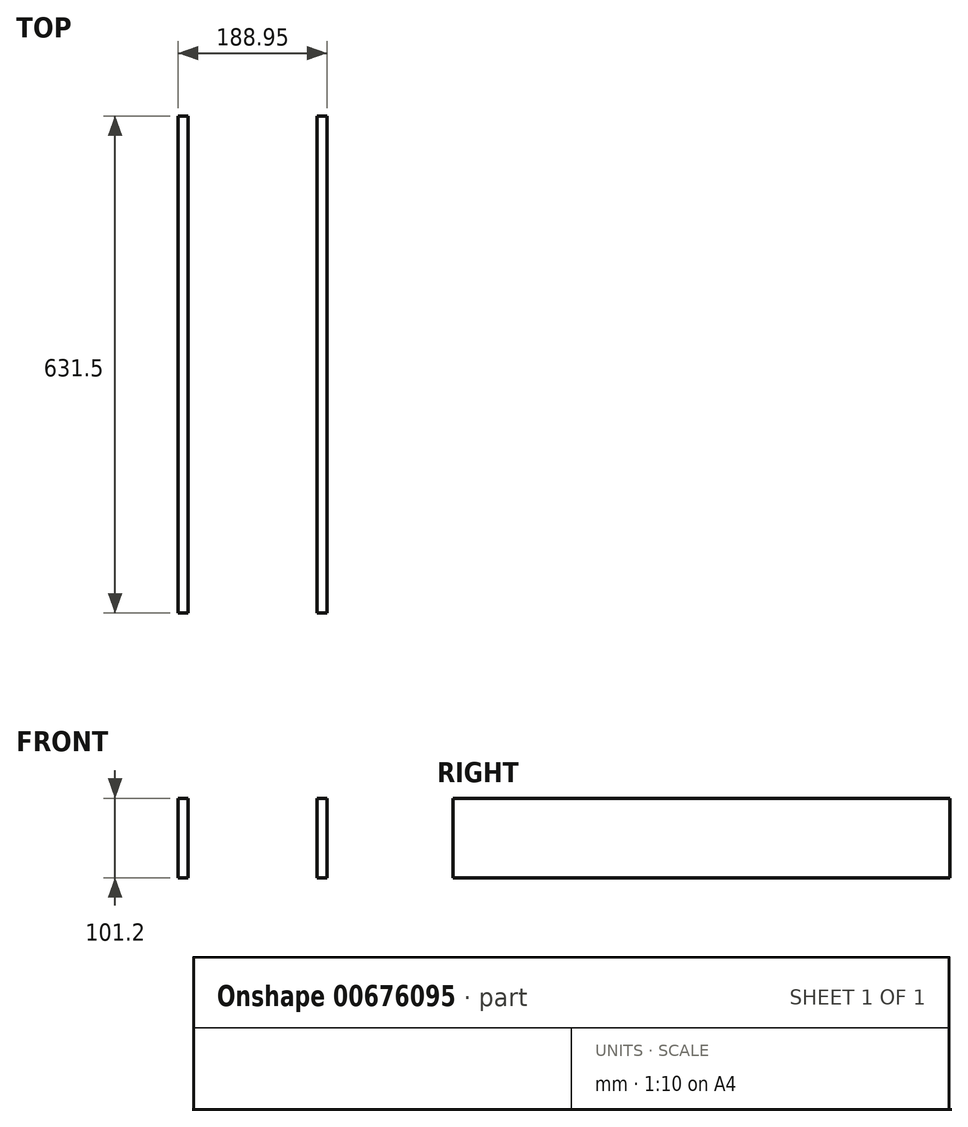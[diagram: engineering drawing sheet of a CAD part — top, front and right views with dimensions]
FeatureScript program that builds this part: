
annotation { "Feature Type Name" : "Feature", "Feature Type Description" : "" }
export const myFeature = defineFeature(function(context is Context, id is Id, definition is map)
    precondition{}
    {
        {
            var Q0;
            Q0=qCreatedBy(makeId("Front.planeOp"),FACE);
            var sketch = newSketch(context, id + "F0", { "sketchPlane" : qUnion([Q0])});
            skLineSegment(sketch, "E0.bottom", {"start": v(0, 0) * mm, "end": v(12.75, 0) * mm});
            skLineSegment(sketch, "E0.top", {"start": v(0, 101.2) * mm, "end": v(12.75, 101.2) * mm});
            skLineSegment(sketch, "E0.left", {"start": v(0, 0) * mm, "end": v(0, 101.2) * mm});
            skLineSegment(sketch, "E0.right", {"start": v(12.75, 0) * mm, "end": v(12.75, 101.2) * mm});
            skLineSegment(sketch, "E1.1.0.0", {"start": v(176.2, 101.2) * mm, "end": v(188.95, 101.2) * mm});
            skLineSegment(sketch, "E1.1.0.1", {"start": v(176.2, 0) * mm, "end": v(176.2, 101.2) * mm});
            skLineSegment(sketch, "E1.1.0.2", {"start": v(188.95, 0) * mm, "end": v(188.95, 101.2) * mm});
            skLineSegment(sketch, "E1.1.0.3", {"start": v(176.2, 0) * mm, "end": v(188.95, 0) * mm});
            skLineSegment(sketch, "E1.direction1", {"start": v(0, 101.2) * mm, "end": v(176.2, 101.2) * mm, "construction": true});
            skSolve(sketch);
        }
        {
            var Q0;
            Q0 = qSketchRegion(id + "F0", true);
            extrude(context, id + "F1", {"entities" : qUnion([Q0]), "depth" : 631.5 * mm, "offsetDistance" : 25 * mm});
        }
    });
